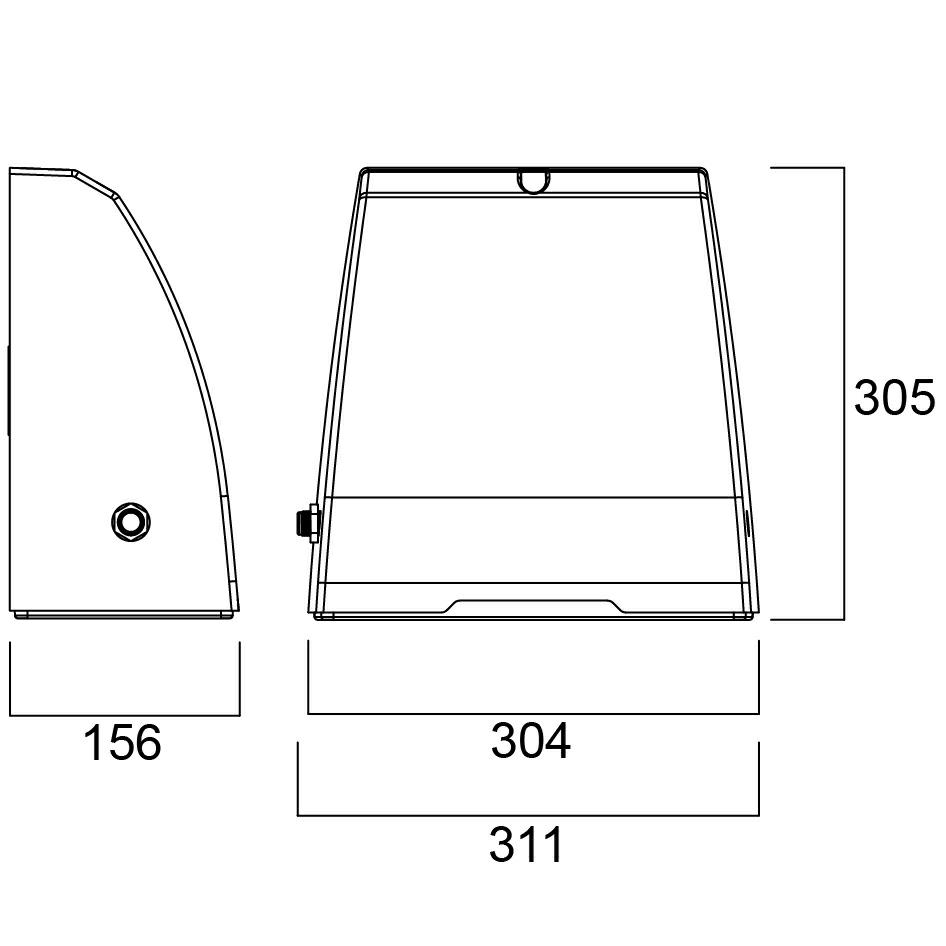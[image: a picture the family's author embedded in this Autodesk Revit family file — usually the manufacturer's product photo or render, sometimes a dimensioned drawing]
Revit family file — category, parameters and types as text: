
# Revit family: 0049945_1900lm
name_source: partatom
category: Lighting Fixtures
revit_build: Autodesk Revit 2018 (Build: 20170223_1515(x64)
units: mm (PartAtom-declared; Revit-internal decimal feet)

## family parameters
Cut with Voids When Loaded = No
Host = Face
Light Source = Yes
OmniClass Number = 23.80.70.00
OmniClass Title = Lighting
Part Type = Normal
Room Calculation Point = No
Round Connector Dimension = Use Diameter
Shared = No

## types (1)
- 0049945 MURO SURF IP65 1700-3250LM 840 PH E3 GR
    Apparent Load = 30 VA
    Assembly Code = D5020200
    AssetType = Fixed
    ClassificationName = Uniclass2015
    ClassificationValue = EF_70_80
    Color Filter = 16777215
    Cost = 0 $
    Default Elevation = 1219 mm
    Description = Muro Surface is a wall mounted fixture for exterior lighting applications with 3 hours combined non-maintained emergency unit. Comes with aluminium housing in RAL7016 anthracite grey colour, frosted PC diffuser, IP65, IK10, Class I, 4000K, non-dimmable multipower driver with 5 settings, 1700 / 1900 / 2750 / 3150 / 3250 lm, 16 / 18 / 26 / 29 / 30 W, up to 109 lm/W total system efficacy, switchable built in Mini photocell, CRI80, Asymmetrical beam, 119.000 hrs L70B50 lifespan, 304 x 305 x 155 mm (L x W x D) dimensions, 4.32 kg weight.
    Dimming Lamp Color Temperature Shift = <None>
    DocumentationLiterature = http://www.sylvania-lighting.com
    ElectricShockClassification = 108
    Emit Shape Visible in Rendering = No
    Emit from Circle Diameter = 610 mm
    IfcExportAs = Class I
    IfcExportType = IfcLightFixtureType
    ImpactProtectionIndex = IfcLightFixtureType
    IngressProtection = IfcLightFixtureType
    InputNominalFrequency = 4000
    InputVoltage = 0
    LampColourRenderingIndex = 16500
    LampColourTemperature = LED
    LampMacAdamStep = 80
    LampNominalLuminous = 4000 K
    LightOutputRatio = LED
    LuminaireType = 0
    ManufacturerName = 108 lm/W
    Material = Feilo Sylvania
    Material_1_SYL = <By Category>
    Material_2_SYL = <By Category>
    Material_3_SYL = <By Category>
    Material_4_SYL = <By Category>
    Model = Muro Surface IP65 1700-3250lm 840 PH E3 Grey
    ModelNumber = 0049945
    ModelReference = Muro Surface IP65 1700-3250lm 840 PH E3 Grey
    Name = Muro Surface IP65 1700-3250lm 840 PH E3 Grey
    NominalDepth = 155 mm  [stored 0.50853 ft]
    NominalHeight = 305 mm  [stored 1.00066 ft]
    NominalLength = 155 mm  [stored 0.50853 ft]
    Photometric Web File = 0049945_1900lm.IES
    PowerConsumption = Lighting
    PowerFactor = 0.95
    Tilt Angle = -90.00°
    Type Image = <None>
    TypeName = Muro Surface IP65 1700-3250lm 840 PH E3 Grey
    URL = 0.9
    Voltage = 0 V
    WarrantyDescription = http://www.sylvania-lighting.com

note: [stored X ft] marks values corroborated as IEEE doubles in the binary element streams (Revit-internal decimal feet)

## geometry (parser evidence)
native form markers: Sweep x1
no freeform markers — native parametric forms only
